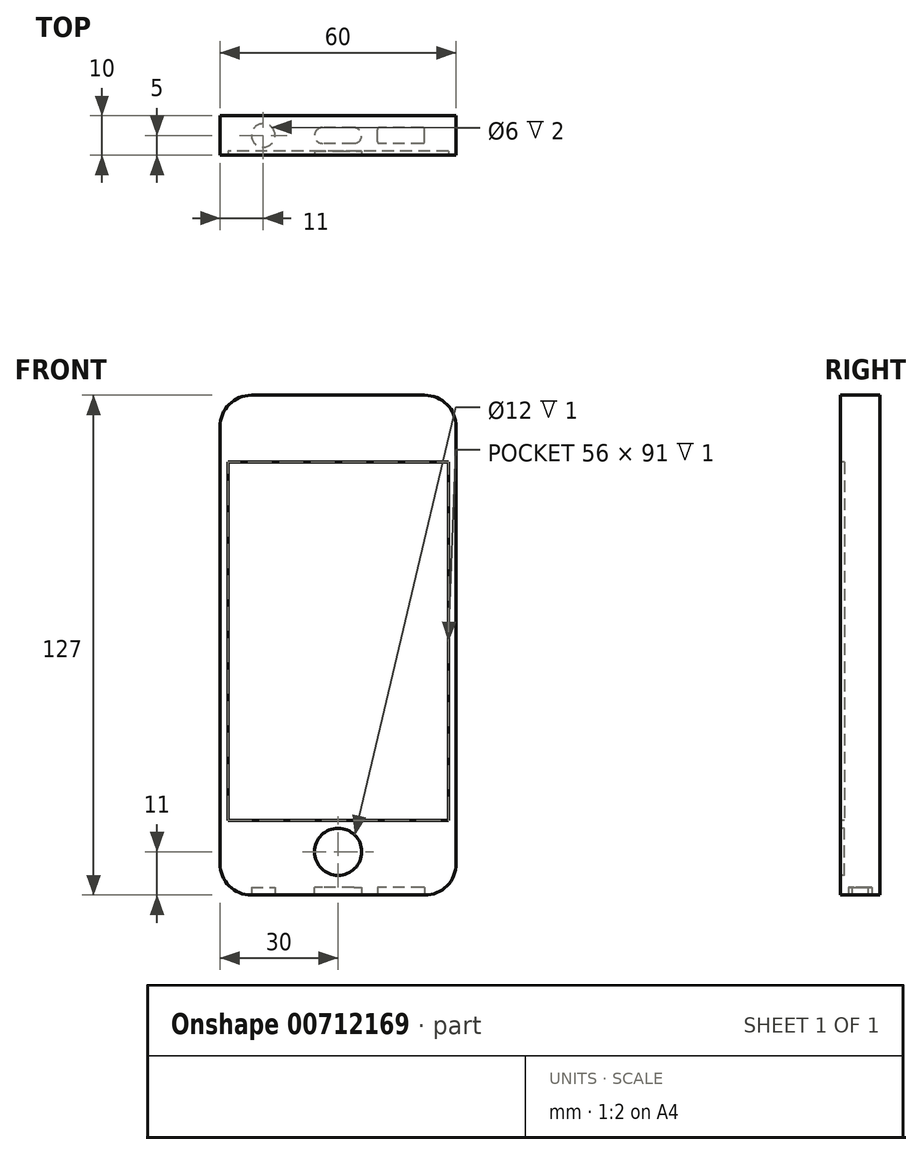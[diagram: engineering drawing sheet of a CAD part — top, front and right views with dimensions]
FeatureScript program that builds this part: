
annotation { "Feature Type Name" : "Feature", "Feature Type Description" : "" }
export const myFeature = defineFeature(function(context is Context, id is Id, definition is map)
    precondition{}
    {
        {
            var Q0;
            Q0=qCreatedBy(makeId("Front.planeOp"),FACE);
            var sketch = newSketch(context, id + "F0", { "sketchPlane" : qUnion([Q0])});
            skLineSegment(sketch, "E0.bottom", {"start": v(30, 63.5) * mm, "end": v(-30, 63.5) * mm});
            skLineSegment(sketch, "E0.top", {"start": v(30, -63.5) * mm, "end": v(-30, -63.5) * mm});
            skLineSegment(sketch, "E0.left", {"start": v(30, 63.5) * mm, "end": v(30, -63.5) * mm});
            skLineSegment(sketch, "E0.right", {"start": v(-30, 63.5) * mm, "end": v(-30, -63.5) * mm});
            skPoint(sketch, "E0.middle", {"position": v(0, 0) * mm});
            skSolve(sketch);
        }
        {
            var Q0;
            Q0=makeQuery(id+"F0.imprint","IMPRINT",FACE,{"disambiguationData":[TD([[makeQuery(id+"F0.imprint","IMPRINT",EDGE,{"derivedFrom":sQuery(id+"F0.wireOp",EDGE,"E0.bottom")}),1.0]])]});
            extrude(context, id + "F1", {"entities" : qUnion([Q0]), "depth" : 10 * mm, "offsetDistance" : 25 * mm});
        }
        {
            var Q0;
            Q0=makeQuery(id+"F1.opExtrude","SWEPT_EDGE",EDGE,{"disambiguationData":[OSD([sQuery(id+"F0.wireOp",EDGE,"E0.bottom"),sQuery(id+"F0.wireOp",EDGE,"E0.left")])]});
            var Q1;
            Q1=makeQuery(id+"F1.opExtrude","SWEPT_EDGE",EDGE,{"disambiguationData":[OSD([sQuery(id+"F0.wireOp",EDGE,"E0.bottom"),sQuery(id+"F0.wireOp",EDGE,"E0.right")])]});
            var Q2;
            Q2=makeQuery(id+"F1.opExtrude","SWEPT_EDGE",EDGE,{"disambiguationData":[OSD([sQuery(id+"F0.wireOp",EDGE,"E0.top"),sQuery(id+"F0.wireOp",EDGE,"E0.left")])]});
            var Q3;
            Q3=makeQuery(id+"F1.opExtrude","SWEPT_EDGE",EDGE,{"disambiguationData":[OSD([sQuery(id+"F0.wireOp",EDGE,"E0.top"),sQuery(id+"F0.wireOp",EDGE,"E0.right")])]});
            fillet(context, id + "F2", {"entities" : qUnion([Q0, Q1, Q2, Q3]), "radius" : 8 * mm, "tangentPropagation" : true, "allowEdgeOverflow" : false});
        }
        {
            var Q0;
            Q0=makeQuery(id+"F1.opExtrude","CAP_FACE",FACE,{"disambiguationData":[OSD([sQuery(id+"F0.wireOp",EDGE,"E0.bottom"),sQuery(id+"F0.wireOp",EDGE,"E0.top"),sQuery(id+"F0.wireOp",EDGE,"E0.left"),sQuery(id+"F0.wireOp",EDGE,"E0.right")])],"isStart":false});
            var sketch = newSketch(context, id + "F3", { "sketchPlane" : qUnion([Q0])});
            skCircle(sketch, "E1", {"center": v(0, -52.5) * mm, "radius": 6 * mm});
            skSolve(sketch);
        }
        {
            var Q0;
            Q0 = qSketchRegion(id + "F3", true);
            extrude(context, id + "F4", {"entities" : qUnion([Q0]), "operationType" : NewBodyOperationType.REMOVE, "oppositeDirection" : true, "depth" : 1 * mm, "offsetDistance" : 25 * mm});
        }
        {
            var Q0;
            Q0=makeQuery(id+"F1.opExtrude","CAP_FACE",FACE,{"disambiguationData":[OSD([sQuery(id+"F0.wireOp",EDGE,"E0.bottom"),sQuery(id+"F0.wireOp",EDGE,"E0.top"),sQuery(id+"F0.wireOp",EDGE,"E0.left"),sQuery(id+"F0.wireOp",EDGE,"E0.right")])],"isStart":false});
            var sketch = newSketch(context, id + "F5", { "sketchPlane" : qUnion([Q0])});
            skLineSegment(sketch, "E2.bottom", {"start": v(28, 46.5) * mm, "end": v(-28, 46.5) * mm});
            skLineSegment(sketch, "E2.top", {"start": v(28, -44.5) * mm, "end": v(-28, -44.5) * mm});
            skLineSegment(sketch, "E2.left", {"start": v(28, 46.5) * mm, "end": v(28, -44.5) * mm});
            skLineSegment(sketch, "E2.right", {"start": v(-28, 46.5) * mm, "end": v(-28, -44.5) * mm});
            skPoint(sketch, "E2.middle", {"position": v(0, 1) * mm});
            skSolve(sketch);
        }
        {
            var Q0;
            Q0=makeQuery(id+"F5.imprint","IMPRINT",FACE,{"disambiguationData":[TD([[makeQuery(id+"F5.imprint","IMPRINT",EDGE,{"derivedFrom":sQuery(id+"F5.wireOp",EDGE,"E2.bottom")}),1.0]])]});
            extrude(context, id + "F6", {"entities" : qUnion([Q0]), "operationType" : NewBodyOperationType.REMOVE, "oppositeDirection" : true, "depth" : 1 * mm, "offsetDistance" : 25 * mm});
        }
        {
            var Q0;
            Q0=makeQuery(id+"F1.opExtrude","SWEPT_FACE",FACE,{"disambiguationData":[OSD([sQuery(id+"F0.wireOp",EDGE,"E0.top")])]});
            var sketch = newSketch(context, id + "F7", { "sketchPlane" : qUnion([Q0])});
            skLineSegment(sketch, "E3.bottom", {"start": v(6, 7) * mm, "end": v(-6, 7) * mm});
            skLineSegment(sketch, "E3.top", {"start": v(6, 3) * mm, "end": v(-6, 3) * mm});
            skLineSegment(sketch, "E3.left", {"start": v(6, 7) * mm, "end": v(6, 3) * mm});
            skLineSegment(sketch, "E3.right", {"start": v(-6, 7) * mm, "end": v(-6, 3) * mm});
            skLineSegment(sketch, "E4.bottom", {"start": v(22, 7) * mm, "end": v(10, 7) * mm});
            skLineSegment(sketch, "E4.top", {"start": v(22, 3) * mm, "end": v(10, 3) * mm});
            skLineSegment(sketch, "E4.left", {"start": v(22, 7) * mm, "end": v(22, 3) * mm});
            skLineSegment(sketch, "E4.right", {"start": v(10, 7) * mm, "end": v(10, 3) * mm});
            skPoint(sketch, "E4.middle", {"position": v(16, 5) * mm});
            skPoint(sketch, "E4.middle.positionSnap0", {"position": v(6, 5) * mm});
            skPoint(sketch, "E4.centerSnap0", {"position": v(6, 5) * mm});
            skCircle(sketch, "E5", {"center": v(-19, 5) * mm, "radius": 3 * mm});
            skPoint(sketch, "E5.centerSnap0", {"position": v(-6, 5) * mm});
            skLineSegment(sketch, "E6", {"start": v(0, 7) * mm, "end": v(0, 10) * mm, "construction": true});
            skSolve(sketch);
        }
        {
            var Q0;
            Q0 = qSketchRegion(id + "F7", true);
            extrude(context, id + "F8", {"entities" : qUnion([Q0]), "operationType" : NewBodyOperationType.REMOVE, "oppositeDirection" : true, "depth" : 2 * mm, "offsetDistance" : 25 * mm});
        }
        {
            var Q0;
            Q0=makeQuery(id+"F8.boolean.opBoolean","COPY",EDGE,{"derivedFrom":makeQuery(id+"F8.opExtrude","SWEPT_EDGE",EDGE,{"disambiguationData":[OSD([sQuery(id+"F7.wireOp",EDGE,"E3.bottom"),sQuery(id+"F7.wireOp",EDGE,"E3.right")])]})});
            var Q1;
            Q1=makeQuery(id+"F8.boolean.opBoolean","COPY",EDGE,{"derivedFrom":makeQuery(id+"F8.opExtrude","SWEPT_EDGE",EDGE,{"disambiguationData":[OSD([sQuery(id+"F7.wireOp",EDGE,"E3.top"),sQuery(id+"F7.wireOp",EDGE,"E3.right")])]})});
            var Q2;
            Q2=makeQuery(id+"F8.boolean.opBoolean","COPY",EDGE,{"derivedFrom":makeQuery(id+"F8.opExtrude","SWEPT_EDGE",EDGE,{"disambiguationData":[OSD([sQuery(id+"F7.wireOp",EDGE,"E3.bottom"),sQuery(id+"F7.wireOp",EDGE,"E3.left")])]})});
            var Q3;
            Q3=makeQuery(id+"F8.boolean.opBoolean","COPY",EDGE,{"derivedFrom":makeQuery(id+"F8.opExtrude","SWEPT_EDGE",EDGE,{"disambiguationData":[OSD([sQuery(id+"F7.wireOp",EDGE,"E3.top"),sQuery(id+"F7.wireOp",EDGE,"E3.left")])]})});
            fillet(context, id + "F9", {"entities" : qUnion([Q0, Q1, Q2, Q3]), "radius" : 2 * mm, "tangentPropagation" : true, "allowEdgeOverflow" : false});
        }
        {
            var Q0;
            Q0=makeQuery(id+"F8.boolean.opBoolean","COPY",EDGE,{"derivedFrom":makeQuery(id+"F8.opExtrude","SWEPT_EDGE",EDGE,{"disambiguationData":[OSD([sQuery(id+"F7.wireOp",EDGE,"E4.bottom"),sQuery(id+"F7.wireOp",EDGE,"E4.right")])]})});
            var Q1;
            Q1=makeQuery(id+"F8.boolean.opBoolean","COPY",EDGE,{"derivedFrom":makeQuery(id+"F8.opExtrude","SWEPT_EDGE",EDGE,{"disambiguationData":[OSD([sQuery(id+"F7.wireOp",EDGE,"E4.top"),sQuery(id+"F7.wireOp",EDGE,"E4.right")])]})});
            var Q2;
            Q2=makeQuery(id+"F8.boolean.opBoolean","COPY",EDGE,{"derivedFrom":makeQuery(id+"F8.opExtrude","SWEPT_EDGE",EDGE,{"disambiguationData":[OSD([sQuery(id+"F0.wireOp",EDGE,"E0.top"),sQuery(id+"F0.wireOp",EDGE,"E0.left"),sQuery(id+"F7.wireOp",EDGE,"E4.top"),sQuery(id+"F7.wireOp",EDGE,"E4.left")])]})});
            var Q3;
            Q3=makeQuery(id+"F8.boolean.opBoolean","COPY",EDGE,{"derivedFrom":makeQuery(id+"F8.opExtrude","SWEPT_EDGE",EDGE,{"disambiguationData":[OSD([sQuery(id+"F0.wireOp",EDGE,"E0.top"),sQuery(id+"F0.wireOp",EDGE,"E0.left"),sQuery(id+"F7.wireOp",EDGE,"E4.bottom"),sQuery(id+"F7.wireOp",EDGE,"E4.left")])]})});
            fillet(context, id + "F10", {"entities" : qUnion([Q0, Q1, Q2, Q3]), "radius" : 0.5 * mm, "tangentPropagation" : true, "allowEdgeOverflow" : false});
        }
    });
